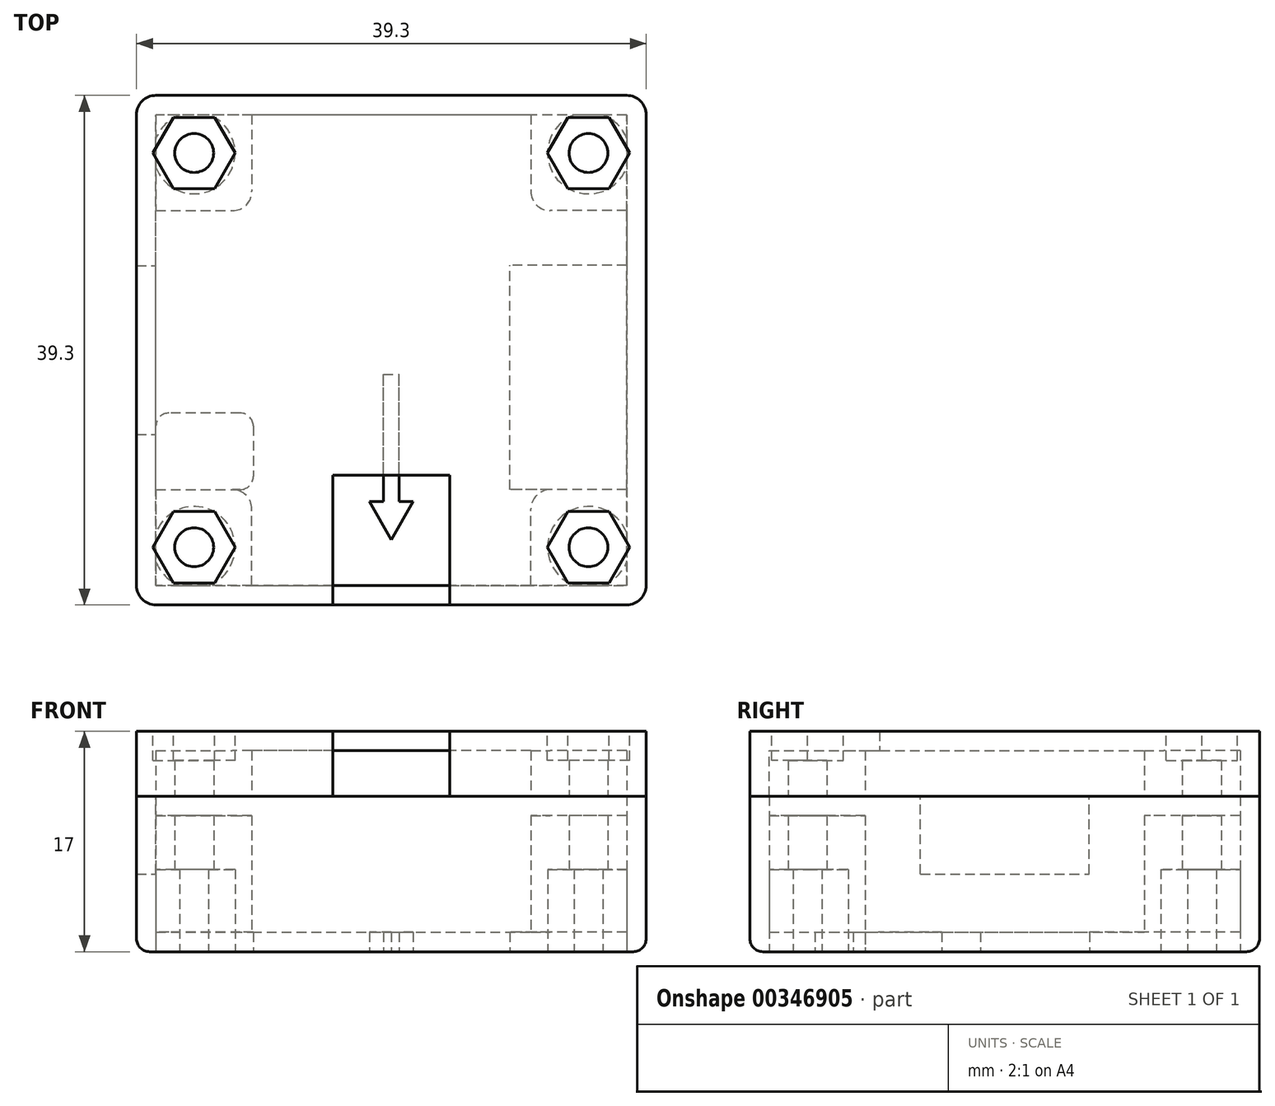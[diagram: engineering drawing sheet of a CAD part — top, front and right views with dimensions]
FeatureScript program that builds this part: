
annotation { "Feature Type Name" : "Feature", "Feature Type Description" : "" }
export const myFeature = defineFeature(function(context is Context, id is Id, definition is map)
    precondition{}
    {
        {
            var Q0;
            Q0=qCreatedBy(makeId("Top.planeOp"),FACE);
            var sketch = newSketch(context, id + "F0", { "sketchPlane" : qUnion([Q0])});
            skLineSegment(sketch, "E0.rect.bottom", {"start": v(18.15, -19.65) * mm, "end": v(-18.15, -19.65) * mm});
            skLineSegment(sketch, "E0.rect.top", {"start": v(18.15, 19.65) * mm, "end": v(-18.15, 19.65) * mm});
            skLineSegment(sketch, "E0.rect.left", {"start": v(19.65, -18.15) * mm, "end": v(19.65, 18.15) * mm});
            skLineSegment(sketch, "E0.rect.right", {"start": v(-19.65, -18.15) * mm, "end": v(-19.65, 18.15) * mm});
            skPoint(sketch, "E0.rect.middle", {"position": v(0, 0) * mm});
            skCircle(sketch, "E1", {"center": v(0, 0) * mm, "radius": 21.5 * mm, "construction": true});
            skLineSegment(sketch, "E2", {"start": v(0, 0) * mm, "end": v(19.65, 19.65) * mm, "construction": true});
            skCircle(sketch, "E3", {"center": v(15.2, 15.2) * mm, "radius": 1.5 * mm});
            skArc(sketch, "E4", {"start": v(14.1, 18.15) * mm, "mid": v(12.98, 12.98) * mm, "end": v(18.15, 14.1) * mm});
            skPoint(sketch, "E5.visualSharp", {"position": v(19.65, 19.65) * mm});
            skArc(sketch, "E5.filletArc", {"start": v(19.65, 18.15) * mm, "mid": v(19.21, 19.21) * mm, "end": v(18.15, 19.65) * mm});
            skLineSegment(sketch, "E6.rect.bottom", {"start": v(18.15, 19.65) * mm, "end": v(10.76, 19.65) * mm});
            skLineSegment(sketch, "E6.rect.top", {"start": v(18.15, 10.76) * mm, "end": v(12.26, 10.76) * mm});
            skLineSegment(sketch, "E6.rect.left", {"start": v(19.65, 18.15) * mm, "end": v(19.65, 10.76) * mm});
            skLineSegment(sketch, "E6.rect.right", {"start": v(10.76, 18.15) * mm, "end": v(10.76, 12.26) * mm});
            skPoint(sketch, "E7.visualSharp", {"position": v(10.76, 10.76) * mm});
            skArc(sketch, "E7.filletArc", {"start": v(10.76, 12.26) * mm, "mid": v(11.2, 11.2) * mm, "end": v(12.26, 10.76) * mm});
            skArc(sketch, "E8.1.1", {"start": v(-16.31, 18.15) * mm, "mid": v(-17.43, 17.43) * mm, "end": v(-18.15, 16.31) * mm});
            skCircle(sketch, "E8.1.2", {"center": v(-15.2, 15.2) * mm, "radius": 1.5 * mm});
            skLineSegment(sketch, "E8.1.3", {"start": v(-18.15, 10.76) * mm, "end": v(-12.26, 10.76) * mm});
            skArc(sketch, "E8.1.4", {"start": v(-12.26, 10.76) * mm, "mid": v(-11.2, 11.2) * mm, "end": v(-10.76, 12.26) * mm});
            skLineSegment(sketch, "E8.1.5", {"start": v(-10.76, 18.15) * mm, "end": v(-10.76, 12.26) * mm});
            skLineSegment(sketch, "E8.1.6", {"start": v(-18.15, 19.65) * mm, "end": v(-10.76, 19.65) * mm});
            skArc(sketch, "E8.1.7", {"start": v(-18.15, 19.65) * mm, "mid": v(-19.21, 19.21) * mm, "end": v(-19.65, 18.15) * mm});
            skLineSegment(sketch, "E8.1.8", {"start": v(-19.65, 18.15) * mm, "end": v(-19.65, 10.76) * mm});
            skArc(sketch, "E8.2.1", {"start": v(-18.15, -16.31) * mm, "mid": v(-17.43, -17.43) * mm, "end": v(-16.31, -18.15) * mm});
            skCircle(sketch, "E8.2.2", {"center": v(-15.2, -15.2) * mm, "radius": 1.5 * mm});
            skLineSegment(sketch, "E8.2.3", {"start": v(-10.76, -18.15) * mm, "end": v(-10.76, -12.26) * mm});
            skArc(sketch, "E8.2.4", {"start": v(-10.76, -12.26) * mm, "mid": v(-11.2, -11.2) * mm, "end": v(-12.26, -10.76) * mm});
            skLineSegment(sketch, "E8.2.5", {"start": v(-18.15, -10.76) * mm, "end": v(-12.26, -10.76) * mm});
            skLineSegment(sketch, "E8.2.6", {"start": v(-19.65, -18.15) * mm, "end": v(-19.65, -10.76) * mm});
            skArc(sketch, "E8.2.7", {"start": v(-19.65, -18.15) * mm, "mid": v(-19.21, -19.21) * mm, "end": v(-18.15, -19.65) * mm});
            skLineSegment(sketch, "E8.2.8", {"start": v(-18.15, -19.65) * mm, "end": v(-10.76, -19.65) * mm});
            skArc(sketch, "E9.2.3.0", {"start": v(18.15, -14.1) * mm, "mid": v(12.98, -12.98) * mm, "end": v(14.1, -18.15) * mm});
            skCircle(sketch, "E9.4.3.0", {"center": v(15.2, -15.2) * mm, "radius": 1.5 * mm});
            skArc(sketch, "E9.9.3.0", {"start": v(12.26, -10.76) * mm, "mid": v(11.2, -11.2) * mm, "end": v(10.76, -12.26) * mm});
            skLineSegment(sketch, "E9.16.3.0", {"start": v(18.15, -19.65) * mm, "end": v(10.76, -19.65) * mm});
            skArc(sketch, "E9.19.3.0", {"start": v(18.15, -19.65) * mm, "mid": v(19.21, -19.21) * mm, "end": v(19.65, -18.15) * mm});
            skLineSegment(sketch, "E9.23.3.0", {"start": v(19.65, -18.15) * mm, "end": v(19.65, -10.76) * mm});
            skPoint(sketch, "E10.orphan", {"position": v(-19.65, 19.65) * mm});
            skPoint(sketch, "E11.orphan", {"position": v(19.65, -19.65) * mm});
            skPoint(sketch, "E12.orphan", {"position": v(-19.65, -19.65) * mm});
            skLineSegment(sketch, "E13.trimOffspring", {"start": v(14.1, 18.15) * mm, "end": v(-14.1, 18.15) * mm});
            skLineSegment(sketch, "E14.trimOffspring", {"start": v(-18.15, -14.1) * mm, "end": v(-18.15, 14.1) * mm});
            skLineSegment(sketch, "E15.trimOffspring", {"start": v(14.1, -18.15) * mm, "end": v(-14.1, -18.15) * mm});
            skLineSegment(sketch, "E16.trimOffspring", {"start": v(18.15, -14.1) * mm, "end": v(18.15, 14.1) * mm});
            skLineSegment(sketch, "E17", {"start": v(-14.1, 18.15) * mm, "end": v(-18.15, 18.15) * mm});
            skLineSegment(sketch, "E18", {"start": v(-18.15, 18.15) * mm, "end": v(-18.15, 14.1) * mm});
            skLineSegment(sketch, "E19", {"start": v(14.1, 18.15) * mm, "end": v(18.15, 18.15) * mm});
            skLineSegment(sketch, "E20", {"start": v(18.15, 18.15) * mm, "end": v(18.15, 14.1) * mm});
            skLineSegment(sketch, "E21", {"start": v(18.15, -14.1) * mm, "end": v(18.15, -18.15) * mm});
            skLineSegment(sketch, "E22", {"start": v(14.1, -18.15) * mm, "end": v(18.15, -18.15) * mm});
            skLineSegment(sketch, "E23", {"start": v(-14.1, -18.15) * mm, "end": v(-18.15, -18.15) * mm});
            skLineSegment(sketch, "E24", {"start": v(-18.15, -14.1) * mm, "end": v(-18.15, -18.15) * mm});
            skLineSegment(sketch, "E25.trimOffspring", {"start": v(18.15, -10.76) * mm, "end": v(12.26, -10.76) * mm});
            skLineSegment(sketch, "E26.trimOffspring", {"start": v(10.76, -18.15) * mm, "end": v(10.76, -12.26) * mm});
            skArc(sketch, "E27.trimOffspring", {"start": v(-18.15, 14.1) * mm, "mid": v(-12.98, 12.98) * mm, "end": v(-14.1, 18.15) * mm});
            skArc(sketch, "E28.trimOffspring", {"start": v(18.15, 16.31) * mm, "mid": v(17.43, 17.43) * mm, "end": v(16.31, 18.15) * mm});
            skArc(sketch, "E29.trimOffspring", {"start": v(16.31, -18.15) * mm, "mid": v(17.43, -17.43) * mm, "end": v(18.15, -16.31) * mm});
            skArc(sketch, "E30.trimOffspring", {"start": v(-14.1, -18.15) * mm, "mid": v(-12.98, -12.98) * mm, "end": v(-18.15, -14.1) * mm});
            skLineSegment(sketch, "E31", {"start": v(-26.46, -4.85) * mm, "end": v(25.33, -4.85) * mm, "construction": true});
            skLineSegment(sketch, "E32", {"start": v(-10.65, -23.17) * mm, "end": v(-10.65, 21.13) * mm, "construction": true});
            skLineSegment(sketch, "E33.bottom", {"start": v(-11.65, -4.85) * mm, "end": v(-17.15, -4.85) * mm});
            skLineSegment(sketch, "E33.top", {"start": v(-11.65, -10.76) * mm, "end": v(-17.15, -10.76) * mm});
            skLineSegment(sketch, "E33.left", {"start": v(-10.65, -5.85) * mm, "end": v(-10.65, -9.76) * mm});
            skLineSegment(sketch, "E33.right", {"start": v(-18.15, -5.85) * mm, "end": v(-18.15, -9.76) * mm});
            skPoint(sketch, "E34.visualSharp", {"position": v(-10.65, -10.76) * mm});
            skArc(sketch, "E34.filletArc", {"start": v(-11.65, -10.76) * mm, "mid": v(-10.94, -10.46) * mm, "end": v(-10.65, -9.76) * mm});
            skPoint(sketch, "E35.visualSharp", {"position": v(-10.65, -4.85) * mm});
            skArc(sketch, "E35.filletArc", {"start": v(-10.65, -5.85) * mm, "mid": v(-10.94, -5.14) * mm, "end": v(-11.65, -4.85) * mm});
            skPoint(sketch, "E36.visualSharp", {"position": v(-18.15, -4.85) * mm});
            skArc(sketch, "E36.filletArc", {"start": v(-17.15, -4.85) * mm, "mid": v(-17.86, -5.14) * mm, "end": v(-18.15, -5.85) * mm});
            skPoint(sketch, "E37.visualSharp", {"position": v(-18.15, -10.76) * mm});
            skArc(sketch, "E37.filletArc", {"start": v(-18.15, -9.76) * mm, "mid": v(-17.86, -10.46) * mm, "end": v(-17.15, -10.76) * mm});
            skLineSegment(sketch, "E38", {"start": v(9.15, -24.31) * mm, "end": v(9.15, 23.94) * mm, "construction": true});
            skLineSegment(sketch, "E39", {"start": v(-23.3, 6.55) * mm, "end": v(24.8, 6.55) * mm, "construction": true});
            skLineSegment(sketch, "E40.bottom", {"start": v(18.15, -10.76) * mm, "end": v(9.15, -10.76) * mm});
            skLineSegment(sketch, "E40.top", {"start": v(18.15, 6.55) * mm, "end": v(9.15, 6.55) * mm});
            skLineSegment(sketch, "E40.left", {"start": v(18.15, -10.76) * mm, "end": v(18.15, 6.55) * mm});
            skLineSegment(sketch, "E40.right", {"start": v(9.15, -10.76) * mm, "end": v(9.15, 6.55) * mm});
            skLineSegment(sketch, "E41", {"start": v(0, -14.62) * mm, "end": v(1.68, -11.69) * mm});
            skLineSegment(sketch, "E42", {"start": v(1.68, -11.69) * mm, "end": v(0.61, -11.69) * mm});
            skLineSegment(sketch, "E43", {"start": v(0.61, -11.69) * mm, "end": v(0.61, -1.87) * mm});
            skLineSegment(sketch, "E44", {"start": v(0.61, -1.87) * mm, "end": v(0, -1.87) * mm});
            skLineSegment(sketch, "E45.MirrorCS", {"start": v(0, -14.62) * mm, "end": v(-1.68, -11.69) * mm});
            skLineSegment(sketch, "E46.MirrorCS", {"start": v(-1.68, -11.69) * mm, "end": v(-0.61, -11.69) * mm});
            skLineSegment(sketch, "E47.MirrorCS", {"start": v(-0.61, -11.69) * mm, "end": v(-0.61, -1.87) * mm});
            skLineSegment(sketch, "E48.MirrorCS", {"start": v(-0.61, -1.87) * mm, "end": v(0, -1.87) * mm});
            skSolve(sketch);
        }
        {
            var Q0;
            Q0=makeQuery(id+"F0.imprint","IMPRINT",FACE,{"disambiguationData":[TD([[makeQuery(id+"F0.imprint","IMPRINT",EDGE,{"derivedFrom":sQuery(id+"F0.wireOp",EDGE,"E0.rect.bottom")}),-1.0]])]});
            extrude(context, id + "F1", {"entities" : qUnion([Q0]), "depth" : 12 * mm});
        }
        {
            var Q0;
            {var subQ2=sQuery(id+"F0.wireOp",EDGE,"E8.1.3");Q0=makeQuery(id+"F0.imprint","IMPRINT",FACE,{"disambiguationData":[TD([[makeQuery(id+"F0.imprint","IMPRINT",EDGE,{"derivedFrom":subQ2}),1.0]])]});}
            var Q1;
            {var subQ3=sQuery(id+"F0.wireOp",EDGE,"E8.1.1");Q1=makeQuery(id+"F0.imprint","IMPRINT",FACE,{"disambiguationData":[TD([[makeQuery(id+"F0.imprint","IMPRINT",EDGE,{"derivedFrom":subQ3}),-1.0]])]});}
            var Q2;
            {var subQ2=sQuery(id+"F0.wireOp",EDGE,"E4");Q2=makeQuery(id+"F0.imprint","IMPRINT",FACE,{"disambiguationData":[TD([[makeQuery(id+"F0.imprint","IMPRINT",EDGE,{"derivedFrom":subQ2}),-1.0]])]});}
            var Q3;
            {var subQ0=sQuery(id+"F0.wireOp",EDGE,"E28.trimOffspring");Q3=makeQuery(id+"F0.imprint","IMPRINT",FACE,{"disambiguationData":[TD([[makeQuery(id+"F0.imprint","IMPRINT",EDGE,{"derivedFrom":subQ0}),-1.0]])]});}
            var Q4;
            {var subQ2=sQuery(id+"F0.wireOp",EDGE,"E8.2.3");Q4=makeQuery(id+"F0.imprint","IMPRINT",FACE,{"disambiguationData":[TD([[makeQuery(id+"F0.imprint","IMPRINT",EDGE,{"derivedFrom":subQ2}),1.0]])]});}
            var Q5;
            {var subQ3=sQuery(id+"F0.wireOp",EDGE,"E8.2.1");Q5=makeQuery(id+"F0.imprint","IMPRINT",FACE,{"disambiguationData":[TD([[makeQuery(id+"F0.imprint","IMPRINT",EDGE,{"derivedFrom":subQ3}),-1.0]])]});}
            var Q6;
            {var subQ3=sQuery(id+"F0.wireOp",EDGE,"E9.2.3.0");Q6=makeQuery(id+"F0.imprint","IMPRINT",FACE,{"disambiguationData":[TD([[makeQuery(id+"F0.imprint","IMPRINT",EDGE,{"derivedFrom":subQ3}),-1.0]])]});}
            var Q7;
            {var subQ0=sQuery(id+"F0.wireOp",EDGE,"E29.trimOffspring");Q7=makeQuery(id+"F0.imprint","IMPRINT",FACE,{"disambiguationData":[TD([[makeQuery(id+"F0.imprint","IMPRINT",EDGE,{"derivedFrom":subQ0}),-1.0]])]});}
            extrude(context, id + "F2", {"entities" : qUnion([Q0, Q1, Q2, Q3, Q4, Q5, Q6, Q7]), "operationType" : NewBodyOperationType.ADD, "depth" : 10.5 * mm});
        }
        {
            var Q0;
            {var subQ2=sQuery(id+"F0.wireOp",EDGE,"E8.1.1");Q0=makeQuery(id+"F0.imprint","IMPRINT",FACE,{"disambiguationData":[TD([[makeQuery(id+"F0.imprint","IMPRINT",EDGE,{"derivedFrom":subQ2}),1.0]])]});}
            var Q1;
            Q1=makeQuery(id+"F0.imprint","IMPRINT",FACE,{"disambiguationData":[TD([[makeQuery(id+"F0.imprint","IMPRINT",EDGE,{"derivedFrom":sQuery(id+"F0.wireOp",EDGE,"E3")}),-1.0]])]});
            var Q2;
            {var subQ2=sQuery(id+"F0.wireOp",EDGE,"E9.2.3.0");Q2=makeQuery(id+"F0.imprint","IMPRINT",FACE,{"disambiguationData":[TD([[makeQuery(id+"F0.imprint","IMPRINT",EDGE,{"derivedFrom":subQ2}),1.0]])]});}
            var Q3;
            {var subQ2=sQuery(id+"F0.wireOp",EDGE,"E8.2.1");Q3=makeQuery(id+"F0.imprint","IMPRINT",FACE,{"disambiguationData":[TD([[makeQuery(id+"F0.imprint","IMPRINT",EDGE,{"derivedFrom":subQ2}),1.0]])]});}
            extrude(context, id + "F3", {"entities" : qUnion([Q0, Q1, Q2, Q3]), "operationType" : NewBodyOperationType.ADD, "depth" : 10.5 * mm, "hasSecondDirection" : true, "secondDirectionOppositeDirection" : false, "secondDirectionDepth" : 6.35 * mm});
        }
        {
            var Q0;
            Q0=qSketchRegion(id+"F0",true);
            var Q1;
            {var subQ2=sQuery(id+"F0.wireOp",EDGE,"E6.rect.top");Q1=makeQuery(id+"F0.imprint","IMPRINT",FACE,{"disambiguationData":[TD([[makeQuery(id+"F0.imprint","IMPRINT",EDGE,{"derivedFrom":subQ2}),1.0]])]});}
            extrude(context, id + "F4", {"entities" : qUnion([Q0, Q1]), "operationType" : NewBodyOperationType.ADD, "depth" : 1.5 * mm});
        }
        {
            var Q0;
            Q0=makeQuery(id+"F0.imprint","IMPRINT",FACE,{"disambiguationData":[TD([[makeQuery(id+"F0.imprint","IMPRINT",EDGE,{"derivedFrom":sQuery(id+"F0.wireOp",EDGE,"E33.bottom")}),1.0]])]});
            extrude(context, id + "F5", {"entities" : qUnion([Q0]), "operationType" : NewBodyOperationType.REMOVE, "depth" : 1.5 * mm});
        }
        {
            var Q0;
            Q0=makeQuery(id+"F0.imprint","IMPRINT",FACE,{"disambiguationData":[TD([[makeQuery(id+"F0.imprint","IMPRINT",EDGE,{"derivedFrom":sQuery(id+"F0.wireOp",EDGE,"E40.top")}),1.0]])]});
            extrude(context, id + "F6", {"entities" : qUnion([Q0]), "operationType" : NewBodyOperationType.REMOVE, "depth" : 1.5 * mm});
        }
        {
            var Q0;
            Q0=makeQuery(id+"F0.imprint","IMPRINT",FACE,{"disambiguationData":[TD([[makeQuery(id+"F0.imprint","IMPRINT",EDGE,{"derivedFrom":sQuery(id+"F0.wireOp",EDGE,"E41")}),1.0]])]});
            extrude(context, id + "F7", {"entities" : qUnion([Q0]), "operationType" : NewBodyOperationType.REMOVE, "depth" : 1.5 * mm});
        }
        {
            var Q0;
            Q0=makeQuery(id+"F1.opExtrude","CAP_FACE",FACE,{"disambiguationData":[OSD([sQuery(id+"F0.wireOp",EDGE,"E0.rect.bottom"),sQuery(id+"F0.wireOp",EDGE,"E0.rect.top"),sQuery(id+"F0.wireOp",EDGE,"E0.rect.left"),sQuery(id+"F0.wireOp",EDGE,"E0.rect.right"),sQuery(id+"F0.wireOp",EDGE,"E5.filletArc"),sQuery(id+"F0.wireOp",EDGE,"E6.rect.bottom"),sQuery(id+"F0.wireOp",EDGE,"E6.rect.left"),sQuery(id+"F0.wireOp",EDGE,"E8.1.6"),sQuery(id+"F0.wireOp",EDGE,"E8.1.7"),sQuery(id+"F0.wireOp",EDGE,"E8.1.8"),sQuery(id+"F0.wireOp",EDGE,"E8.2.6"),sQuery(id+"F0.wireOp",EDGE,"E8.2.7"),sQuery(id+"F0.wireOp",EDGE,"E8.2.8"),sQuery(id+"F0.wireOp",EDGE,"E9.16.3.0"),sQuery(id+"F0.wireOp",EDGE,"E9.19.3.0"),sQuery(id+"F0.wireOp",EDGE,"E9.23.3.0"),sQuery(id+"F0.wireOp",EDGE,"E13.trimOffspring"),sQuery(id+"F0.wireOp",EDGE,"E14.trimOffspring"),sQuery(id+"F0.wireOp",EDGE,"E15.trimOffspring"),sQuery(id+"F0.wireOp",EDGE,"E16.trimOffspring"),sQuery(id+"F0.wireOp",EDGE,"E17"),sQuery(id+"F0.wireOp",EDGE,"E18"),sQuery(id+"F0.wireOp",EDGE,"E19"),sQuery(id+"F0.wireOp",EDGE,"E20"),sQuery(id+"F0.wireOp",EDGE,"E21"),sQuery(id+"F0.wireOp",EDGE,"E22"),sQuery(id+"F0.wireOp",EDGE,"E23"),sQuery(id+"F0.wireOp",EDGE,"E24"),sQuery(id+"F0.wireOp",EDGE,"E33.right"),sQuery(id+"F0.wireOp",EDGE,"E40.left")])],"isStart":false});
            var sketch = newSketch(context, id + "F8", { "sketchPlane" : qUnion([Q0])});
            skLineSegment(sketch, "E49.bottom", {"start": v(-19.65, 6.5) * mm, "end": v(-18.15, 6.5) * mm});
            skLineSegment(sketch, "E49.top", {"start": v(-19.65, -6.5) * mm, "end": v(-18.15, -6.5) * mm});
            skLineSegment(sketch, "E49.left", {"start": v(-19.65, 6.5) * mm, "end": v(-19.65, -6.5) * mm});
            skLineSegment(sketch, "E49.right", {"start": v(-18.15, 6.5) * mm, "end": v(-18.15, -6.5) * mm});
            skLineSegment(sketch, "E50", {"start": v(-25.19, 6.5) * mm, "end": v(-14.9, 6.5) * mm, "construction": true});
            skSolve(sketch);
        }
        {
            var Q0;
            Q0=qSketchRegion(id+"F8",true);
            extrude(context, id + "F9", {"entities" : qUnion([Q0]), "operationType" : NewBodyOperationType.REMOVE, "oppositeDirection" : true, "depth" : 6 * mm});
        }
        {
            var Q0;
            Q0=makeQuery(id+"F1.opExtrude","CAP_EDGE",EDGE,{"disambiguationData":[OSD([sQuery(id+"F0.wireOp",EDGE,"E0.rect.left"),sQuery(id+"F0.wireOp",EDGE,"E6.rect.left"),sQuery(id+"F0.wireOp",EDGE,"E9.23.3.0")])],"isStart":true});
            fillet(context, id + "F10", {"entities" : qUnion([Q0]), "radius" : 1 * mm, "tangentPropagation" : true, "allowEdgeOverflow" : false});
        }
        {
            var Q0;
            Q0=makeQuery(id+"F1.opExtrude","CAP_FACE",FACE,{"disambiguationData":[OSD([sQuery(id+"F0.wireOp",EDGE,"E0.rect.bottom"),sQuery(id+"F0.wireOp",EDGE,"E0.rect.top"),sQuery(id+"F0.wireOp",EDGE,"E0.rect.left"),sQuery(id+"F0.wireOp",EDGE,"E0.rect.right"),sQuery(id+"F0.wireOp",EDGE,"E5.filletArc"),sQuery(id+"F0.wireOp",EDGE,"E6.rect.bottom"),sQuery(id+"F0.wireOp",EDGE,"E6.rect.left"),sQuery(id+"F0.wireOp",EDGE,"E8.1.6"),sQuery(id+"F0.wireOp",EDGE,"E8.1.7"),sQuery(id+"F0.wireOp",EDGE,"E8.1.8"),sQuery(id+"F0.wireOp",EDGE,"E8.2.6"),sQuery(id+"F0.wireOp",EDGE,"E8.2.7"),sQuery(id+"F0.wireOp",EDGE,"E8.2.8"),sQuery(id+"F0.wireOp",EDGE,"E9.16.3.0"),sQuery(id+"F0.wireOp",EDGE,"E9.19.3.0"),sQuery(id+"F0.wireOp",EDGE,"E9.23.3.0"),sQuery(id+"F0.wireOp",EDGE,"E13.trimOffspring"),sQuery(id+"F0.wireOp",EDGE,"E14.trimOffspring"),sQuery(id+"F0.wireOp",EDGE,"E15.trimOffspring"),sQuery(id+"F0.wireOp",EDGE,"E16.trimOffspring"),sQuery(id+"F0.wireOp",EDGE,"E17"),sQuery(id+"F0.wireOp",EDGE,"E18"),sQuery(id+"F0.wireOp",EDGE,"E19"),sQuery(id+"F0.wireOp",EDGE,"E20"),sQuery(id+"F0.wireOp",EDGE,"E21"),sQuery(id+"F0.wireOp",EDGE,"E22"),sQuery(id+"F0.wireOp",EDGE,"E23"),sQuery(id+"F0.wireOp",EDGE,"E24"),sQuery(id+"F0.wireOp",EDGE,"E33.right"),sQuery(id+"F0.wireOp",EDGE,"E40.left")])],"isStart":false});
            cPlane(context, id + "F11", {"entities" : qUnion([Q0]), "cplaneType" : CPlaneType.OFFSET, "offset" : 0 * mm, "width" : 150 * mm, "height" : 150 * mm});
        }
        {
            var Q0;
            Q0=qCreatedBy(id+"F11.planeOp",FACE);
            var sketch = newSketch(context, id + "F12", { "sketchPlane" : qUnion([Q0])});
            skLineSegment(sketch, "E51.rect.bottom", {"start": v(18.15, -19.65) * mm, "end": v(-18.15, -19.65) * mm});
            skLineSegment(sketch, "E51.rect.top", {"start": v(18.15, 19.65) * mm, "end": v(-18.15, 19.65) * mm});
            skLineSegment(sketch, "E51.rect.left", {"start": v(19.65, -18.15) * mm, "end": v(19.65, 18.15) * mm});
            skLineSegment(sketch, "E51.rect.right", {"start": v(-19.65, -18.15) * mm, "end": v(-19.65, 18.15) * mm});
            skPoint(sketch, "E51.rect.middle", {"position": v(0, 0) * mm});
            skCircle(sketch, "E52", {"center": v(0, 0) * mm, "radius": 21.5 * mm, "construction": true});
            skLineSegment(sketch, "E53", {"start": v(0, 0) * mm, "end": v(19.65, 19.65) * mm, "construction": true});
            skCircle(sketch, "E54", {"center": v(15.2, 15.2) * mm, "radius": 1.5 * mm});
            skArc(sketch, "E55", {"start": v(14.1, 18.15) * mm, "mid": v(12.98, 12.98) * mm, "end": v(18.15, 14.1) * mm});
            skPoint(sketch, "E56.visualSharp", {"position": v(19.65, 19.65) * mm});
            skArc(sketch, "E56.filletArc", {"start": v(19.65, 18.15) * mm, "mid": v(19.21, 19.21) * mm, "end": v(18.15, 19.65) * mm});
            skLineSegment(sketch, "E57.rect.bottom", {"start": v(18.15, 19.65) * mm, "end": v(10.76, 19.65) * mm});
            skLineSegment(sketch, "E57.rect.top", {"start": v(18.15, 10.76) * mm, "end": v(12.26, 10.76) * mm});
            skLineSegment(sketch, "E57.rect.left", {"start": v(19.65, 18.15) * mm, "end": v(19.65, 10.76) * mm});
            skLineSegment(sketch, "E57.rect.right", {"start": v(10.76, 18.15) * mm, "end": v(10.76, 12.26) * mm});
            skPoint(sketch, "E58.visualSharp", {"position": v(10.76, 10.76) * mm});
            skArc(sketch, "E58.filletArc", {"start": v(10.76, 12.26) * mm, "mid": v(11.2, 11.2) * mm, "end": v(12.26, 10.76) * mm});
            skArc(sketch, "E59.1.1", {"start": v(-16.31, 18.15) * mm, "mid": v(-17.43, 17.43) * mm, "end": v(-18.15, 16.31) * mm});
            skCircle(sketch, "E59.1.2", {"center": v(-15.2, 15.2) * mm, "radius": 1.5 * mm});
            skLineSegment(sketch, "E59.1.3", {"start": v(-18.15, 10.76) * mm, "end": v(-12.26, 10.76) * mm});
            skArc(sketch, "E59.1.4", {"start": v(-12.26, 10.76) * mm, "mid": v(-11.2, 11.2) * mm, "end": v(-10.76, 12.26) * mm});
            skLineSegment(sketch, "E59.1.5", {"start": v(-10.76, 18.15) * mm, "end": v(-10.76, 12.26) * mm});
            skLineSegment(sketch, "E59.1.6", {"start": v(-18.15, 19.65) * mm, "end": v(-10.76, 19.65) * mm});
            skArc(sketch, "E59.1.7", {"start": v(-18.15, 19.65) * mm, "mid": v(-19.21, 19.21) * mm, "end": v(-19.65, 18.15) * mm});
            skLineSegment(sketch, "E59.1.8", {"start": v(-19.65, 18.15) * mm, "end": v(-19.65, 10.76) * mm});
            skArc(sketch, "E59.2.1", {"start": v(-18.15, -16.31) * mm, "mid": v(-17.43, -17.43) * mm, "end": v(-16.31, -18.15) * mm});
            skCircle(sketch, "E59.2.2", {"center": v(-15.2, -15.2) * mm, "radius": 1.5 * mm});
            skLineSegment(sketch, "E59.2.3", {"start": v(-10.76, -18.15) * mm, "end": v(-10.76, -12.26) * mm});
            skArc(sketch, "E59.2.4", {"start": v(-10.76, -12.26) * mm, "mid": v(-11.2, -11.2) * mm, "end": v(-12.26, -10.76) * mm});
            skLineSegment(sketch, "E59.2.5", {"start": v(-18.15, -10.76) * mm, "end": v(-12.26, -10.76) * mm});
            skLineSegment(sketch, "E59.2.6", {"start": v(-19.65, -18.15) * mm, "end": v(-19.65, -10.76) * mm});
            skArc(sketch, "E59.2.7", {"start": v(-19.65, -18.15) * mm, "mid": v(-19.21, -19.21) * mm, "end": v(-18.15, -19.65) * mm});
            skLineSegment(sketch, "E59.2.8", {"start": v(-18.15, -19.65) * mm, "end": v(-10.76, -19.65) * mm});
            skArc(sketch, "E60.2.3.0", {"start": v(18.15, -14.1) * mm, "mid": v(12.98, -12.98) * mm, "end": v(14.1, -18.15) * mm});
            skCircle(sketch, "E60.4.3.0", {"center": v(15.2, -15.2) * mm, "radius": 1.5 * mm});
            skArc(sketch, "E60.9.3.0", {"start": v(12.26, -10.76) * mm, "mid": v(11.2, -11.2) * mm, "end": v(10.76, -12.26) * mm});
            skLineSegment(sketch, "E60.16.3.0", {"start": v(18.15, -19.65) * mm, "end": v(10.76, -19.65) * mm});
            skArc(sketch, "E60.19.3.0", {"start": v(18.15, -19.65) * mm, "mid": v(19.21, -19.21) * mm, "end": v(19.65, -18.15) * mm});
            skLineSegment(sketch, "E60.23.3.0", {"start": v(19.65, -18.15) * mm, "end": v(19.65, -10.76) * mm});
            skPoint(sketch, "E61.orphan", {"position": v(-19.65, 19.65) * mm});
            skPoint(sketch, "E62.orphan", {"position": v(19.65, -19.65) * mm});
            skPoint(sketch, "E63.orphan", {"position": v(-19.65, -19.65) * mm});
            skLineSegment(sketch, "E64.trimOffspring", {"start": v(14.1, 18.15) * mm, "end": v(-14.1, 18.15) * mm});
            skLineSegment(sketch, "E65.trimOffspring", {"start": v(-18.15, -14.1) * mm, "end": v(-18.15, 14.1) * mm});
            skLineSegment(sketch, "E66.trimOffspring", {"start": v(14.1, -18.15) * mm, "end": v(-14.1, -18.15) * mm});
            skLineSegment(sketch, "E67.trimOffspring", {"start": v(18.15, -14.1) * mm, "end": v(18.15, 14.1) * mm});
            skLineSegment(sketch, "E68", {"start": v(-14.1, 18.15) * mm, "end": v(-18.15, 18.15) * mm});
            skLineSegment(sketch, "E69", {"start": v(-18.15, 18.15) * mm, "end": v(-18.15, 14.1) * mm});
            skLineSegment(sketch, "E70", {"start": v(14.1, 18.15) * mm, "end": v(18.15, 18.15) * mm});
            skLineSegment(sketch, "E71", {"start": v(18.15, 18.15) * mm, "end": v(18.15, 14.1) * mm});
            skLineSegment(sketch, "E72", {"start": v(18.15, -14.1) * mm, "end": v(18.15, -18.15) * mm});
            skLineSegment(sketch, "E73", {"start": v(14.1, -18.15) * mm, "end": v(18.15, -18.15) * mm});
            skLineSegment(sketch, "E74", {"start": v(-14.1, -18.15) * mm, "end": v(-18.15, -18.15) * mm});
            skLineSegment(sketch, "E75", {"start": v(-18.15, -14.1) * mm, "end": v(-18.15, -18.15) * mm});
            skLineSegment(sketch, "E76.trimOffspring", {"start": v(18.15, -10.76) * mm, "end": v(12.26, -10.76) * mm});
            skLineSegment(sketch, "E77.trimOffspring", {"start": v(10.76, -18.15) * mm, "end": v(10.76, -12.26) * mm});
            skArc(sketch, "E78.trimOffspring", {"start": v(-18.15, 14.1) * mm, "mid": v(-12.98, 12.98) * mm, "end": v(-14.1, 18.15) * mm});
            skArc(sketch, "E79.trimOffspring", {"start": v(18.15, 16.31) * mm, "mid": v(17.43, 17.43) * mm, "end": v(16.31, 18.15) * mm});
            skArc(sketch, "E80.trimOffspring", {"start": v(16.31, -18.15) * mm, "mid": v(17.43, -17.43) * mm, "end": v(18.15, -16.31) * mm});
            skArc(sketch, "E81.trimOffspring", {"start": v(-14.1, -18.15) * mm, "mid": v(-12.98, -12.98) * mm, "end": v(-18.15, -14.1) * mm});
            skLineSegment(sketch, "E82", {"start": v(-26.46, -4.85) * mm, "end": v(25.33, -4.85) * mm, "construction": true});
            skLineSegment(sketch, "E83", {"start": v(-10.65, -23.17) * mm, "end": v(-10.65, 21.13) * mm, "construction": true});
            skLineSegment(sketch, "E84.right", {"start": v(-18.15, -5.85) * mm, "end": v(-18.15, -9.76) * mm});
            skPoint(sketch, "E85.visualSharp", {"position": v(-10.65, -10.76) * mm});
            skPoint(sketch, "E86.visualSharp", {"position": v(-10.65, -4.85) * mm});
            skPoint(sketch, "E87.visualSharp", {"position": v(-18.15, -4.85) * mm});
            skPoint(sketch, "E88.visualSharp", {"position": v(-18.15, -10.76) * mm});
            skLineSegment(sketch, "E89", {"start": v(9.15, -24.31) * mm, "end": v(9.15, 23.94) * mm, "construction": true});
            skLineSegment(sketch, "E90", {"start": v(-23.3, 6.55) * mm, "end": v(24.8, 6.55) * mm, "construction": true});
            skLineSegment(sketch, "E91.left", {"start": v(18.15, -10.76) * mm, "end": v(18.15, 6.55) * mm});
            skSolve(sketch);
        }
        {
            var Q0;
            Q0=makeQuery(id+"F12.imprint","IMPRINT",FACE,{"disambiguationData":[TD([[makeQuery(id+"F12.imprint","IMPRINT",EDGE,{"derivedFrom":sQuery(id+"F12.wireOp",EDGE,"E51.rect.bottom")}),-1.0]])]});
            var Q1;
            {var subQ2=sQuery(id+"F12.wireOp",EDGE,"E55");Q1=makeQuery(id+"F12.imprint","IMPRINT",FACE,{"disambiguationData":[TD([[makeQuery(id+"F12.imprint","IMPRINT",EDGE,{"derivedFrom":subQ2}),-1.0]])]});}
            var Q2;
            {var subQ5=sQuery(id+"F12.wireOp",EDGE,"E60.2.3.0");Q2=makeQuery(id+"F12.imprint","IMPRINT",FACE,{"disambiguationData":[TD([[makeQuery(id+"F12.imprint","IMPRINT",EDGE,{"derivedFrom":subQ5}),-1.0]])]});}
            var Q3;
            {var subQ2=sQuery(id+"F12.wireOp",EDGE,"E59.1.3");Q3=makeQuery(id+"F12.imprint","IMPRINT",FACE,{"disambiguationData":[TD([[makeQuery(id+"F12.imprint","IMPRINT",EDGE,{"derivedFrom":subQ2}),1.0]])]});}
            var Q4;
            {var subQ2=sQuery(id+"F12.wireOp",EDGE,"E59.2.3");Q4=makeQuery(id+"F12.imprint","IMPRINT",FACE,{"disambiguationData":[TD([[makeQuery(id+"F12.imprint","IMPRINT",EDGE,{"derivedFrom":subQ2}),1.0]])]});}
            var Q5;
            {var subQ0=sQuery(id+"F12.wireOp",EDGE,"E79.trimOffspring");Q5=makeQuery(id+"F12.imprint","IMPRINT",FACE,{"disambiguationData":[TD([[makeQuery(id+"F12.imprint","IMPRINT",EDGE,{"derivedFrom":subQ0}),-1.0]])]});}
            var Q6;
            {var subQ3=sQuery(id+"F12.wireOp",EDGE,"E59.1.1");Q6=makeQuery(id+"F12.imprint","IMPRINT",FACE,{"disambiguationData":[TD([[makeQuery(id+"F12.imprint","IMPRINT",EDGE,{"derivedFrom":subQ3}),-1.0]])]});}
            var Q7;
            {var subQ0=sQuery(id+"F12.wireOp",EDGE,"E80.trimOffspring");Q7=makeQuery(id+"F12.imprint","IMPRINT",FACE,{"disambiguationData":[TD([[makeQuery(id+"F12.imprint","IMPRINT",EDGE,{"derivedFrom":subQ0}),-1.0]])]});}
            var Q8;
            {var subQ3=sQuery(id+"F12.wireOp",EDGE,"E59.2.1");Q8=makeQuery(id+"F12.imprint","IMPRINT",FACE,{"disambiguationData":[TD([[makeQuery(id+"F12.imprint","IMPRINT",EDGE,{"derivedFrom":subQ3}),-1.0]])]});}
            var Q9;
            {var subQ9=sQuery(id+"F12.wireOp",EDGE,"E57.rect.top");Q9=makeQuery(id+"F12.imprint","IMPRINT",FACE,{"disambiguationData":[TD([[makeQuery(id+"F12.imprint","IMPRINT",EDGE,{"derivedFrom":subQ9}),1.0]])]});}
            var Q10;
            {var subQ2=sQuery(id+"F12.wireOp",EDGE,"E59.2.1");Q10=makeQuery(id+"F12.imprint","IMPRINT",FACE,{"disambiguationData":[TD([[makeQuery(id+"F12.imprint","IMPRINT",EDGE,{"derivedFrom":subQ2}),1.0]])]});}
            var Q11;
            {var subQ2=sQuery(id+"F12.wireOp",EDGE,"E60.2.3.0");Q11=makeQuery(id+"F12.imprint","IMPRINT",FACE,{"disambiguationData":[TD([[makeQuery(id+"F12.imprint","IMPRINT",EDGE,{"derivedFrom":subQ2}),1.0]])]});}
            var Q12;
            Q12=makeQuery(id+"F12.imprint","IMPRINT",FACE,{"disambiguationData":[TD([[makeQuery(id+"F12.imprint","IMPRINT",EDGE,{"derivedFrom":sQuery(id+"F12.wireOp",EDGE,"E54")}),-1.0]])]});
            var Q13;
            {var subQ2=sQuery(id+"F12.wireOp",EDGE,"E59.1.1");Q13=makeQuery(id+"F12.imprint","IMPRINT",FACE,{"disambiguationData":[TD([[makeQuery(id+"F12.imprint","IMPRINT",EDGE,{"derivedFrom":subQ2}),1.0]])]});}
            extrude(context, id + "F13", {"entities" : qUnion([Q0, Q1, Q2, Q3, Q4, Q5, Q6, Q7, Q8, Q9, Q10, Q11, Q12, Q13]), "depth" : 5 * mm});
        }
        {
            var Q0;
            {var subQ9=sQuery(id+"F12.wireOp",EDGE,"E57.rect.top");Q0=makeQuery(id+"F12.imprint","IMPRINT",FACE,{"disambiguationData":[TD([[makeQuery(id+"F12.imprint","IMPRINT",EDGE,{"derivedFrom":subQ9}),1.0]])]});}
            extrude(context, id + "F14", {"entities" : qUnion([Q0]), "operationType" : NewBodyOperationType.REMOVE, "depth" : 3.5 * mm});
        }
        {
            var Q0;
            Q0=makeQuery(id+"F13.opExtrude","CAP_FACE",FACE,{"disambiguationData":[OSD([sQuery(id+"F12.wireOp",EDGE,"E51.rect.bottom"),sQuery(id+"F12.wireOp",EDGE,"E51.rect.top"),sQuery(id+"F12.wireOp",EDGE,"E51.rect.left"),sQuery(id+"F12.wireOp",EDGE,"E51.rect.right"),sQuery(id+"F12.wireOp",EDGE,"E54"),sQuery(id+"F12.wireOp",EDGE,"E56.filletArc"),sQuery(id+"F12.wireOp",EDGE,"E57.rect.bottom"),sQuery(id+"F12.wireOp",EDGE,"E57.rect.left"),sQuery(id+"F12.wireOp",EDGE,"E59.1.2"),sQuery(id+"F12.wireOp",EDGE,"E59.1.6"),sQuery(id+"F12.wireOp",EDGE,"E59.1.7"),sQuery(id+"F12.wireOp",EDGE,"E59.1.8"),sQuery(id+"F12.wireOp",EDGE,"E59.2.2"),sQuery(id+"F12.wireOp",EDGE,"E59.2.6"),sQuery(id+"F12.wireOp",EDGE,"E59.2.7"),sQuery(id+"F12.wireOp",EDGE,"E59.2.8"),sQuery(id+"F12.wireOp",EDGE,"E60.4.3.0"),sQuery(id+"F12.wireOp",EDGE,"E60.16.3.0"),sQuery(id+"F12.wireOp",EDGE,"E60.19.3.0"),sQuery(id+"F12.wireOp",EDGE,"E60.23.3.0")])],"isStart":false});
            cPlane(context, id + "F15", {"entities" : qUnion([Q0]), "cplaneType" : CPlaneType.OFFSET, "offset" : 0 * mm, "width" : 150 * mm, "height" : 150 * mm});
        }
        {
            var Q0;
            Q0=qCreatedBy(id+"F15.planeOp",FACE);
            var sketch = newSketch(context, id + "F16", { "sketchPlane" : qUnion([Q0])});
            skCircle(sketch, "E92.cCircle", {"center": v(-15.2, 15.2) * mm, "radius": 2.75 * mm, "construction": true});
            skLineSegment(sketch, "E92.0", {"start": v(-16.8, 17.95) * mm, "end": v(-13.62, 17.95) * mm});
            skLineSegment(sketch, "E92.1", {"start": v(-13.62, 17.95) * mm, "end": v(-12.03, 15.2) * mm});
            skLineSegment(sketch, "E92.2", {"start": v(-12.03, 15.2) * mm, "end": v(-13.62, 12.45) * mm});
            skLineSegment(sketch, "E92.3", {"start": v(-13.62, 12.45) * mm, "end": v(-16.8, 12.45) * mm});
            skLineSegment(sketch, "E92.4", {"start": v(-16.8, 12.45) * mm, "end": v(-18.38, 15.2) * mm});
            skLineSegment(sketch, "E92.5", {"start": v(-18.38, 15.2) * mm, "end": v(-16.8, 17.95) * mm});
            skPoint(sketch, "E92.0.midPoint", {"position": v(-15.2, 17.95) * mm});
            skLineSegment(sketch, "E93.MirrorCS", {"start": v(13.62, 17.95) * mm, "end": v(12.03, 15.2) * mm});
            skLineSegment(sketch, "E94.MirrorCS", {"start": v(16.8, 17.95) * mm, "end": v(13.62, 17.95) * mm});
            skLineSegment(sketch, "E95.MirrorCS", {"start": v(18.38, 15.2) * mm, "end": v(16.8, 17.95) * mm});
            skLineSegment(sketch, "E96.MirrorCS", {"start": v(16.8, 12.45) * mm, "end": v(18.38, 15.2) * mm});
            skLineSegment(sketch, "E97.MirrorCS", {"start": v(13.62, 12.45) * mm, "end": v(16.8, 12.45) * mm});
            skLineSegment(sketch, "E98.MirrorCS", {"start": v(12.03, 15.2) * mm, "end": v(13.62, 12.45) * mm});
            skCircle(sketch, "E99.cCircle", {"center": v(-15.2, -15.2) * mm, "radius": 2.75 * mm, "construction": true});
            skLineSegment(sketch, "E99.0", {"start": v(-16.8, -12.45) * mm, "end": v(-13.62, -12.45) * mm});
            skLineSegment(sketch, "E99.1", {"start": v(-13.62, -12.45) * mm, "end": v(-12.03, -15.2) * mm});
            skLineSegment(sketch, "E99.2", {"start": v(-12.03, -15.2) * mm, "end": v(-13.62, -17.95) * mm});
            skLineSegment(sketch, "E99.3", {"start": v(-13.62, -17.95) * mm, "end": v(-16.8, -17.95) * mm});
            skLineSegment(sketch, "E99.4", {"start": v(-16.8, -17.95) * mm, "end": v(-18.38, -15.2) * mm});
            skLineSegment(sketch, "E99.5", {"start": v(-18.38, -15.2) * mm, "end": v(-16.8, -12.45) * mm});
            skPoint(sketch, "E99.0.midPoint", {"position": v(-15.2, -12.45) * mm});
            skLineSegment(sketch, "E100.MirrorCS", {"start": v(16.8, -12.45) * mm, "end": v(13.62, -12.45) * mm});
            skLineSegment(sketch, "E101.MirrorCS", {"start": v(13.62, -12.45) * mm, "end": v(12.03, -15.2) * mm});
            skLineSegment(sketch, "E102.MirrorCS", {"start": v(12.03, -15.2) * mm, "end": v(13.62, -17.95) * mm});
            skLineSegment(sketch, "E103.MirrorCS", {"start": v(13.62, -17.95) * mm, "end": v(16.8, -17.95) * mm});
            skLineSegment(sketch, "E104.MirrorCS", {"start": v(16.8, -17.95) * mm, "end": v(18.38, -15.2) * mm});
            skLineSegment(sketch, "E105.MirrorCS", {"start": v(18.38, -15.2) * mm, "end": v(16.8, -12.45) * mm});
            skSolve(sketch);
        }
        {
            var Q0;
            Q0=qSketchRegion(id+"F16",true);
            extrude(context, id + "F17", {"entities" : qUnion([Q0]), "operationType" : NewBodyOperationType.REMOVE, "oppositeDirection" : true, "depth" : 2.25 * mm});
        }
        {
            var Q0;
            Q0=qCreatedBy(id+"F11.planeOp",FACE);
            var sketch = newSketch(context, id + "F18", { "sketchPlane" : qUnion([Q0])});
            skLineSegment(sketch, "E106.rect.bottom", {"start": v(4.5, -9.65) * mm, "end": v(-4.5, -9.65) * mm});
            skLineSegment(sketch, "E106.rect.top", {"start": v(4.5, -19.65) * mm, "end": v(-4.5, -19.65) * mm});
            skLineSegment(sketch, "E106.rect.left", {"start": v(4.5, -9.65) * mm, "end": v(4.5, -19.65) * mm});
            skLineSegment(sketch, "E106.rect.right", {"start": v(-4.5, -9.65) * mm, "end": v(-4.5, -19.65) * mm});
            skPoint(sketch, "E106.rect.middle", {"position": v(0, -14.65) * mm});
            skSolve(sketch);
        }
        {
            var Q0;
            Q0=qSketchRegion(id+"F18",true);
            var Q1;
            Q1=makeQuery(id+"F13.opExtrude","CAP_FACE",FACE,{"disambiguationData":[OSD([sQuery(id+"F12.wireOp",EDGE,"E51.rect.bottom"),sQuery(id+"F12.wireOp",EDGE,"E51.rect.top"),sQuery(id+"F12.wireOp",EDGE,"E51.rect.left"),sQuery(id+"F12.wireOp",EDGE,"E51.rect.right"),sQuery(id+"F12.wireOp",EDGE,"E54"),sQuery(id+"F12.wireOp",EDGE,"E56.filletArc"),sQuery(id+"F12.wireOp",EDGE,"E57.rect.bottom"),sQuery(id+"F12.wireOp",EDGE,"E57.rect.left"),sQuery(id+"F12.wireOp",EDGE,"E59.1.2"),sQuery(id+"F12.wireOp",EDGE,"E59.1.6"),sQuery(id+"F12.wireOp",EDGE,"E59.1.7"),sQuery(id+"F12.wireOp",EDGE,"E59.1.8"),sQuery(id+"F12.wireOp",EDGE,"E59.2.2"),sQuery(id+"F12.wireOp",EDGE,"E59.2.6"),sQuery(id+"F12.wireOp",EDGE,"E59.2.7"),sQuery(id+"F12.wireOp",EDGE,"E59.2.8"),sQuery(id+"F12.wireOp",EDGE,"E60.4.3.0"),sQuery(id+"F12.wireOp",EDGE,"E60.16.3.0"),sQuery(id+"F12.wireOp",EDGE,"E60.19.3.0"),sQuery(id+"F12.wireOp",EDGE,"E60.23.3.0")])],"isStart":false});
            extrude(context, id + "F19", {"entities" : qUnion([Q0]), "operationType" : NewBodyOperationType.REMOVE, "endBound" : BoundingType.UP_TO_SURFACE, "endBoundEntityFace" : qUnion([Q1]), "depth" : 25 * mm});
        }
    });
